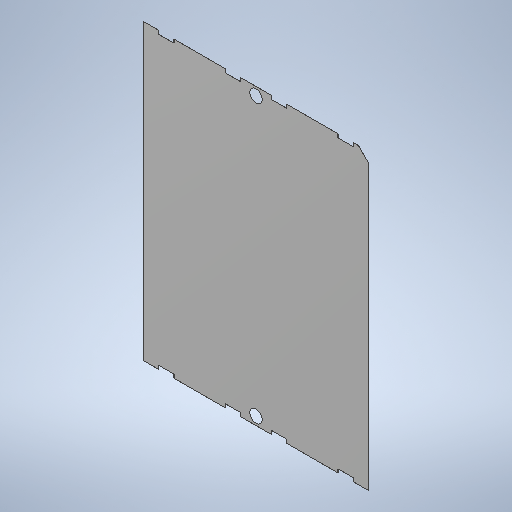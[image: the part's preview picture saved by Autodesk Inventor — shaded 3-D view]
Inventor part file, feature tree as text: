
AUTODESK INVENTOR PART (.ipt)
format: ipt  version: 2025 (Build 290162000, 162)  size: 245,248 bytes
history: native  units: mm
features: extrude x1, sketch x1, imported_body x1
ambient origin geometry x8: Origin, YZ Plane, XZ Plane, XY Plane, X Axis, Y Axis, Z Axis, Center Point
bodies: Solid1 (feature_tree)
feature tree (3):
  extrude  "Extrusion1"  Depth=44.099993mm
  sketch  "Sketch1"  dims[d0=0.0mm d1=0.0mm d2=2.4mm d3=44.099993mm d4=22.049997mm d5=1.6mm d6=2.4mm d7=1.6mm]
  imported_body  "Base1"
